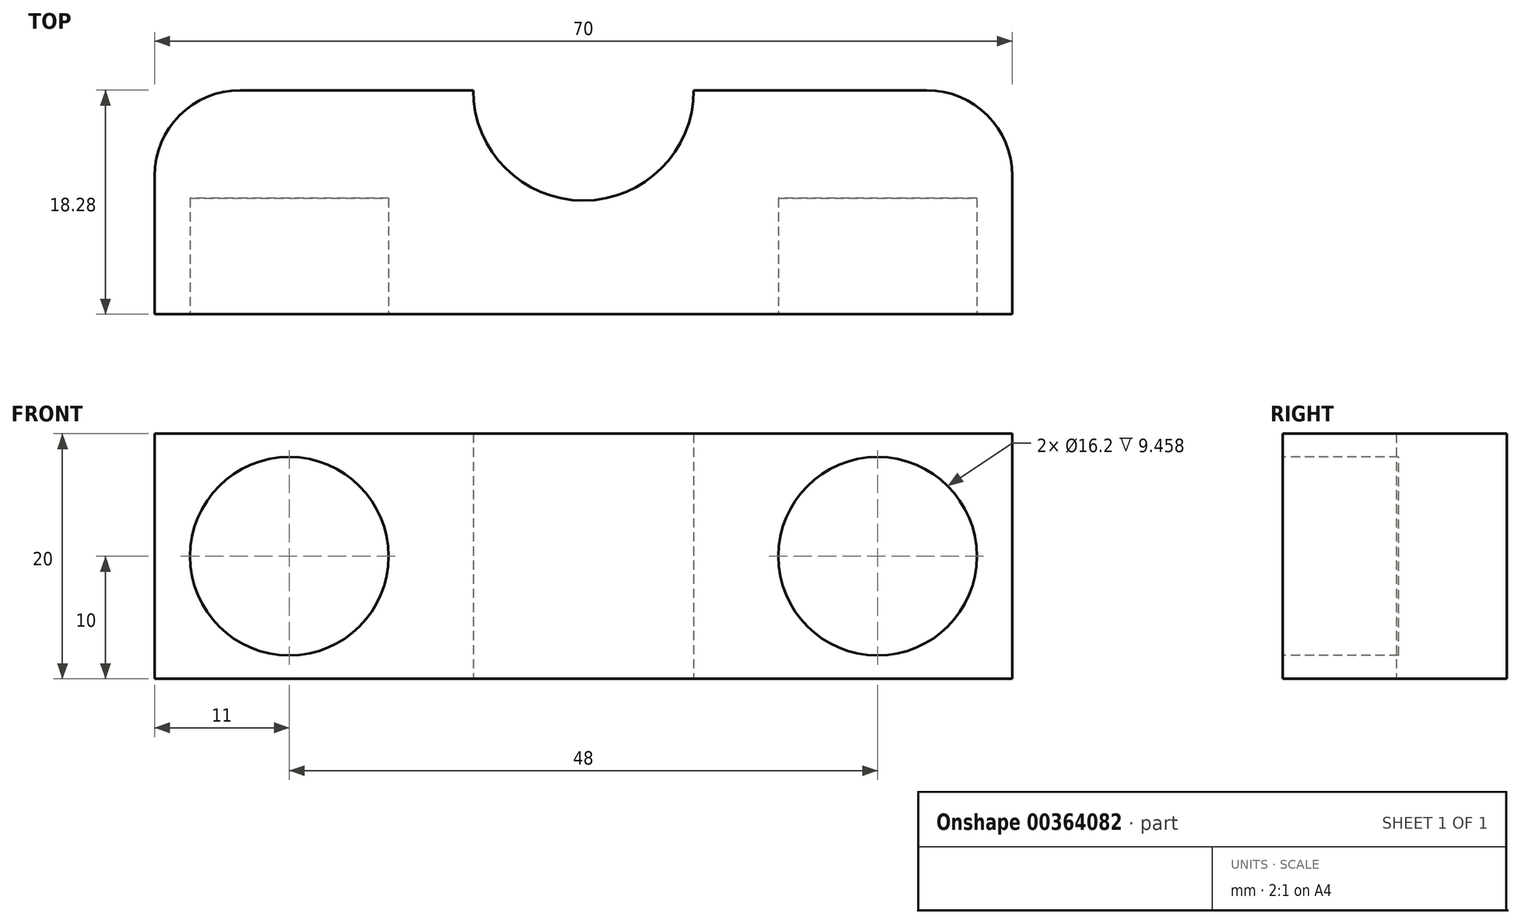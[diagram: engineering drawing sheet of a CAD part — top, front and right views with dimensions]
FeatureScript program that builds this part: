
annotation { "Feature Type Name" : "Feature", "Feature Type Description" : "" }
export const myFeature = defineFeature(function(context is Context, id is Id, definition is map)
    precondition{}
    {
        {
            var Q0;
            Q0=qCreatedBy(makeId("Top.planeOp"),FACE);
            var sketch = newSketch(context, id + "F0", { "sketchPlane" : qUnion([Q0])});
            skLineSegment(sketch, "E0.bottom", {"start": v(-35, 8.82) * mm, "end": v(35, 8.82) * mm});
            skLineSegment(sketch, "E0.top", {"start": v(-35, -9.46) * mm, "end": v(35, -9.46) * mm});
            skLineSegment(sketch, "E0.left", {"start": v(-35, 8.82) * mm, "end": v(-35, -9.46) * mm});
            skLineSegment(sketch, "E0.right", {"start": v(35, 8.82) * mm, "end": v(35, -9.46) * mm});
            skSolve(sketch);
        }
        {
            var Q0;
            Q0 = qSketchRegion(id + "F0", true);
            extrude(context, id + "F1", {"entities" : qUnion([Q0]), "depth" : 20 * mm});
        }
        {
            var Q0;
            Q0=qCreatedBy(makeId("Front.planeOp"),FACE);
            cPlane(context, id + "F2", {"entities" : qUnion([Q0]), "cplaneType" : CPlaneType.OFFSET, "offset" : 10 * mm, "width" : 150 * mm, "height" : 150 * mm});
        }
        {
            var Q0;
            Q0=qCreatedBy(id+"F2.planeOp",FACE);
            var sketch = newSketch(context, id + "F3", { "sketchPlane" : qUnion([Q0])});
            skCircle(sketch, "E1", {"center": v(-24, 10) * mm, "radius": 8.1 * mm});
            skCircle(sketch, "E2.MirrorC", {"center": v(24, 10) * mm, "radius": 8.1 * mm});
            skSolve(sketch);
        }
        {
            var Q0;
            Q0 = qSketchRegion(id + "F3", true);
            extrude(context, id + "F4", {"entities" : qUnion([Q0]), "operationType" : NewBodyOperationType.REMOVE, "oppositeDirection" : true, "depth" : 10 * mm});
        }
        {
            var Q0;
            Q0=qCreatedBy(makeId("Top.planeOp"),FACE);
            var sketch = newSketch(context, id + "F5", { "sketchPlane" : qUnion([Q0])});
            skCircle(sketch, "E3", {"center": v(0, 8.82) * mm, "radius": 9 * mm});
            skSolve(sketch);
        }
        {
            var Q0;
            Q0 = qSketchRegion(id + "F5", true);
            extrude(context, id + "F6", {"entities" : qUnion([Q0]), "operationType" : NewBodyOperationType.REMOVE, "depth" : 25 * mm});
        }
        {
            var Q0;
            Q0=makeQuery(id+"F1.opExtrude","SWEPT_EDGE",EDGE,{"disambiguationData":[OSD([sQuery(id+"F0.wireOp",EDGE,"E0.bottom"),sQuery(id+"F0.wireOp",EDGE,"E0.right")])]});
            var Q1;
            Q1=makeQuery(id+"F1.opExtrude","SWEPT_EDGE",EDGE,{"disambiguationData":[OSD([sQuery(id+"F0.wireOp",EDGE,"E0.bottom"),sQuery(id+"F0.wireOp",EDGE,"E0.left")])]});
            fillet(context, id + "F7", {"entities" : qUnion([Q0, Q1]), "radius" : 7 * mm, "tangentPropagation" : true, "allowEdgeOverflow" : false});
        }
    });
